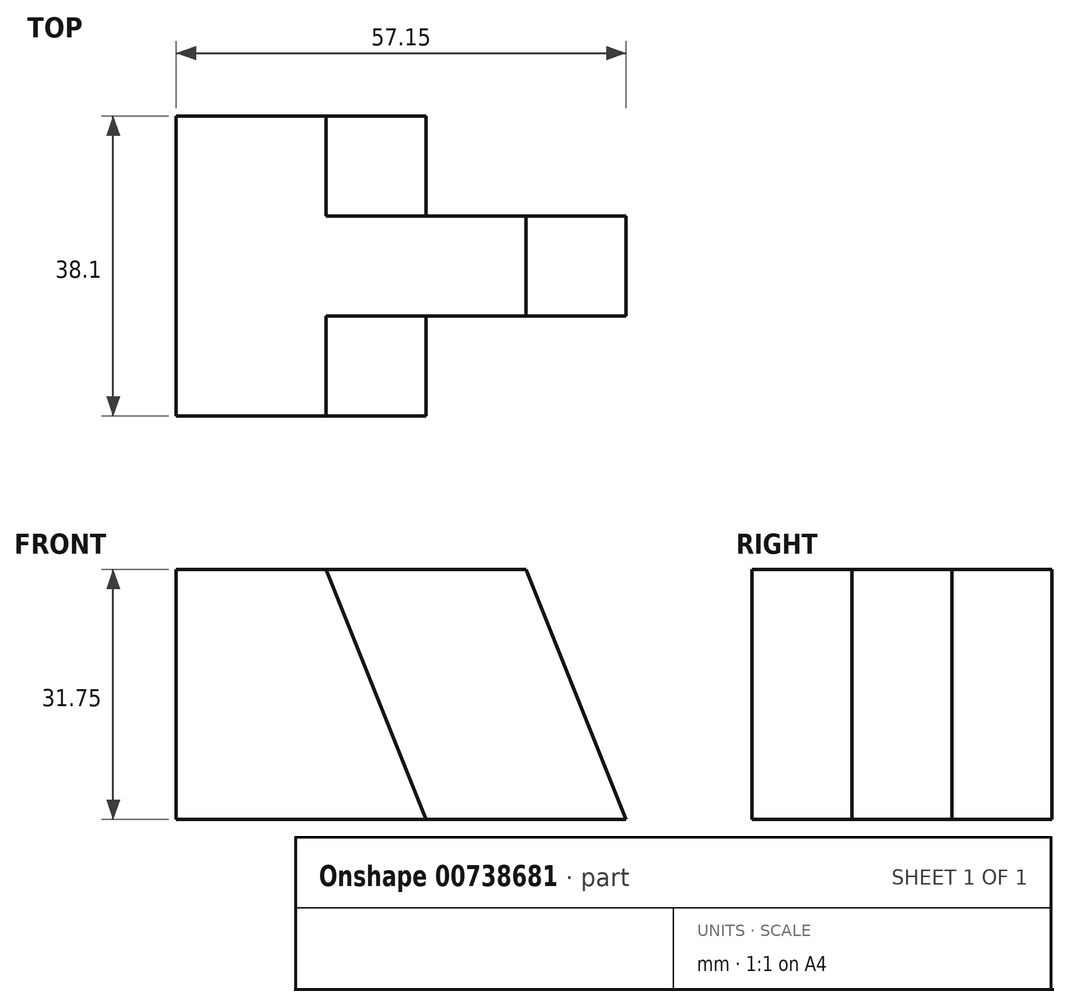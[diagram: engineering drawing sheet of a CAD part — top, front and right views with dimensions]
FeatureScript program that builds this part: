
annotation { "Feature Type Name" : "Feature", "Feature Type Description" : "" }
export const myFeature = defineFeature(function(context is Context, id is Id, definition is map)
    precondition{}
    {
        {
            var Q0;
            Q0=qCreatedBy(makeId("Front.planeOp"),FACE);
            var sketch = newSketch(context, id + "F0", { "sketchPlane" : qUnion([Q0])});
            skLineSegment(sketch, "E0", {"start": v(0, 0) * mm, "end": v(57.15, 0) * mm});
            skLineSegment(sketch, "E1", {"start": v(57.15, 0) * mm, "end": v(57.15, 31.75) * mm});
            skLineSegment(sketch, "E2", {"start": v(57.15, 31.75) * mm, "end": v(0, 31.75) * mm});
            skLineSegment(sketch, "E3", {"start": v(0, 31.75) * mm, "end": v(0, 0) * mm});
            skSolve(sketch);
        }
        {
            var Q0;
            Q0=makeQuery(id+"F0.imprint","IMPRINT",FACE,{"disambiguationData":[TD([[makeQuery(id+"F0.imprint","IMPRINT",EDGE,{"derivedFrom":sQuery(id+"F0.wireOp",EDGE,"E0")}),1.0]])]});
            extrude(context, id + "F1", {"entities" : qUnion([Q0]), "depth" : 38.1 * mm, "offsetDistance" : 25.4 * mm});
        }
        {
            var Q0;
            Q0=makeQuery(id+"F1.opExtrude","CAP_FACE",FACE,{"disambiguationData":[OSD([sQuery(id+"F0.wireOp",EDGE,"E0"),sQuery(id+"F0.wireOp",EDGE,"E1"),sQuery(id+"F0.wireOp",EDGE,"E2"),sQuery(id+"F0.wireOp",EDGE,"E3")])],"isStart":false});
            var sketch = newSketch(context, id + "F2", { "sketchPlane" : qUnion([Q0])});
            skLineSegment(sketch, "E4", {"start": v(0, 31.75) * mm, "end": v(19.05, 31.75) * mm});
            skLineSegment(sketch, "E5", {"start": v(57.15, 0) * mm, "end": v(31.75, 0) * mm});
            skLineSegment(sketch, "E6", {"start": v(31.75, 0) * mm, "end": v(19.05, 31.75) * mm});
            skSolve(sketch);
        }
        {
            var Q0;
            Q0=makeQuery(id+"F2.imprint","IMPRINT",FACE,{"disambiguationData":[TD([[makeQuery(id+"F2.imprint","IMPRINT",EDGE,{"derivedFrom":sQuery(id+"F2.wireOp",EDGE,"E5")}),1.0]])]});
            extrude(context, id + "F3", {"entities" : qUnion([Q0]), "operationType" : NewBodyOperationType.REMOVE, "oppositeDirection" : true, "depth" : 12.7 * mm, "offsetDistance" : 25.4 * mm});
        }
        {
            var Q0;
            Q0=makeQuery(id+"F3.boolean.opBoolean","COPY",FACE,{"derivedFrom":makeQuery(id+"F3.opExtrude","CAP_FACE",FACE,{"disambiguationData":[OSD([sQuery(id+"F0.wireOp",EDGE,"E1"),sQuery(id+"F0.wireOp",EDGE,"E2"),sQuery(id+"F2.wireOp",EDGE,"E5"),sQuery(id+"F2.wireOp",EDGE,"E6")])],"isStart":false})});
            var sketch = newSketch(context, id + "F4", { "sketchPlane" : qUnion([Q0])});
            skLineSegment(sketch, "E7", {"start": v(19.05, 31.75) * mm, "end": v(44.45, 31.75) * mm});
            skLineSegment(sketch, "E8", {"start": v(44.45, 31.75) * mm, "end": v(57.15, 0) * mm});
            skSolve(sketch);
        }
        {
            var Q0;
            {var subQ0=sQuery(id+"F4.wireOp",EDGE,"E8");Q0=makeQuery(id+"F4.imprint","IMPRINT",FACE,{"disambiguationData":[TD([[makeQuery(id+"F4.imprint","IMPRINT",EDGE,{"derivedFrom":subQ0}),1.0]])]});}
            extrude(context, id + "F5", {"entities" : qUnion([Q0]), "operationType" : NewBodyOperationType.REMOVE, "oppositeDirection" : true, "depth" : 12.7 * mm, "offsetDistance" : 25.4 * mm});
        }
        {
            var Q0;
            Q0=makeQuery(id+"F1.opExtrude","CAP_FACE",FACE,{"disambiguationData":[OSD([sQuery(id+"F0.wireOp",EDGE,"E0"),sQuery(id+"F0.wireOp",EDGE,"E1"),sQuery(id+"F0.wireOp",EDGE,"E2"),sQuery(id+"F0.wireOp",EDGE,"E3")])],"isStart":true});
            var sketch = newSketch(context, id + "F6", { "sketchPlane" : qUnion([Q0])});
            skLineSegment(sketch, "E9", {"start": v(0, 31.75) * mm, "end": v(-19.05, 31.75) * mm});
            skLineSegment(sketch, "E10", {"start": v(-57.15, 0) * mm, "end": v(-31.75, 0) * mm});
            skLineSegment(sketch, "E11", {"start": v(-31.75, 0) * mm, "end": v(-19.05, 31.75) * mm});
            skLineSegment(sketch, "E12", {"start": v(-19.05, 31.75) * mm, "end": v(-44.45, 31.75) * mm});
            skLineSegment(sketch, "E13", {"start": v(-44.45, 31.75) * mm, "end": v(-57.15, 0) * mm});
            skSolve(sketch);
        }
        {
            var Q0;
            Q0=makeQuery(id+"F6.imprint","IMPRINT",FACE,{"disambiguationData":[TD([[makeQuery(id+"F6.imprint","IMPRINT",EDGE,{"derivedFrom":sQuery(id+"F6.wireOp",EDGE,"E10")}),-1.0]])]});
            var Q1;
            {var subQ0=sQuery(id+"F6.wireOp",EDGE,"E13");Q1=makeQuery(id+"F6.imprint","IMPRINT",FACE,{"disambiguationData":[TD([[makeQuery(id+"F6.imprint","IMPRINT",EDGE,{"derivedFrom":subQ0}),-1.0]])]});}
            extrude(context, id + "F7", {"entities" : qUnion([Q0, Q1]), "operationType" : NewBodyOperationType.REMOVE, "oppositeDirection" : true, "depth" : 12.7 * mm, "offsetDistance" : 25.4 * mm});
        }
    });
